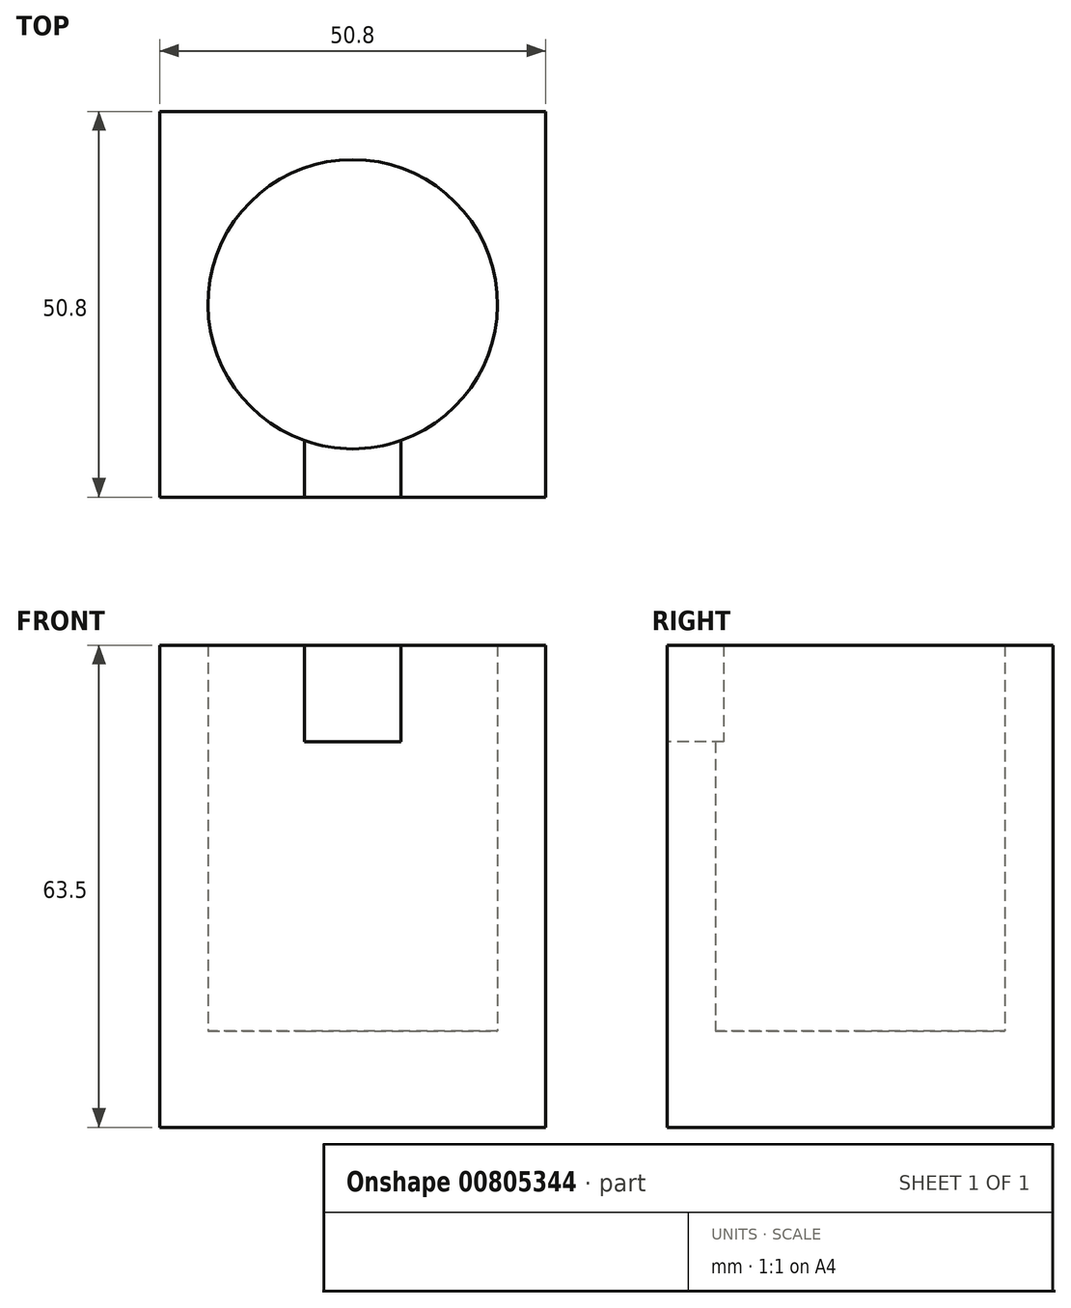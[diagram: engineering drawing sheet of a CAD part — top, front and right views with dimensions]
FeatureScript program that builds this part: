
annotation { "Feature Type Name" : "Feature", "Feature Type Description" : "" }
export const myFeature = defineFeature(function(context is Context, id is Id, definition is map)
    precondition{}
    {
        {
            var Q0;
            Q0=qCreatedBy(makeId("Top.planeOp"),FACE);
            var sketch = newSketch(context, id + "F0", { "sketchPlane" : qUnion([Q0])});
            skLineSegment(sketch, "E0.bottom", {"start": v(-50.8, 50.8) * mm, "end": v(0, 50.8) * mm});
            skLineSegment(sketch, "E0.top", {"start": v(-50.8, 0) * mm, "end": v(0, 0) * mm});
            skLineSegment(sketch, "E0.left", {"start": v(-50.8, 50.8) * mm, "end": v(-50.8, 0) * mm});
            skLineSegment(sketch, "E0.right", {"start": v(0, 50.8) * mm, "end": v(0, 0) * mm});
            skLineSegment(sketch, "E1", {"start": v(0, 25.4) * mm, "end": v(0, 0) * mm});
            skLineSegment(sketch, "E2", {"start": v(0, 0) * mm, "end": v(-25.4, 0) * mm});
            skCircle(sketch, "E3", {"center": v(-25.4, 25.4) * mm, "radius": 19.05 * mm});
            skSolve(sketch);
        }
        {
            var Q0;
            Q0=makeQuery(id+"F0.imprint","IMPRINT",FACE,{"disambiguationData":[TD([[makeQuery(id+"F0.imprint","IMPRINT",EDGE,{"derivedFrom":sQuery(id+"F0.wireOp",EDGE,"E0.bottom")}),-1.0]])]});
            extrude(context, id + "F1", {"entities" : qUnion([Q0]), "depth" : 63.5 * mm, "offsetDistance" : 25.4 * mm});
        }
        {
            var Q0;
            Q0=makeQuery(id+"F0.imprint","IMPRINT",FACE,{"disambiguationData":[TD([[makeQuery(id+"F0.imprint","IMPRINT",EDGE,{"derivedFrom":sQuery(id+"F0.wireOp",EDGE,"E3")}),1.0]])]});
            extrude(context, id + "F2", {"entities" : qUnion([Q0]), "operationType" : NewBodyOperationType.ADD, "depth" : 12.7 * mm, "offsetDistance" : 25.4 * mm});
        }
        {
            var Q0;
            Q0=makeQuery(id+"F1.opExtrude","SWEPT_FACE",FACE,{"disambiguationData":[OSD([sQuery(id+"F0.wireOp",EDGE,"E0.top"),sQuery(id+"F0.wireOp",EDGE,"E2")])]});
            var sketch = newSketch(context, id + "F3", { "sketchPlane" : qUnion([Q0])});
            skLineSegment(sketch, "E4", {"start": v(0, 63.5) * mm, "end": v(-25.4, 63.5) * mm});
            skLineSegment(sketch, "E5", {"start": v(-25.4, 63.5) * mm, "end": v(-19.05, 63.5) * mm});
            skLineSegment(sketch, "E6", {"start": v(-19.05, 63.5) * mm, "end": v(-25.4, 63.5) * mm});
            skLineSegment(sketch, "E7", {"start": v(-31.75, 63.5) * mm, "end": v(-25.4, 63.5) * mm});
            skLineSegment(sketch, "E8", {"start": v(-25.4, 63.5) * mm, "end": v(-25.4, 50.8) * mm});
            skLineSegment(sketch, "E9.top", {"start": v(-31.75, 50.8) * mm, "end": v(-25.4, 50.8) * mm});
            skLineSegment(sketch, "E9.left", {"start": v(-31.75, 63.5) * mm, "end": v(-31.75, 50.8) * mm});
            skLineSegment(sketch, "E10.bottom", {"start": v(-25.4, 50.8) * mm, "end": v(-19.05, 50.8) * mm});
            skLineSegment(sketch, "E10.right", {"start": v(-19.05, 50.8) * mm, "end": v(-19.05, 63.5) * mm});
            skLineSegment(sketch, "E11.bottom", {"start": v(-19.05, 50.8) * mm, "end": v(-31.75, 50.8) * mm});
            skLineSegment(sketch, "E11.top", {"start": v(-19.05, 63.5) * mm, "end": v(-31.75, 63.5) * mm});
            skLineSegment(sketch, "E11.right", {"start": v(-31.75, 50.8) * mm, "end": v(-31.75, 63.5) * mm});
            skSolve(sketch);
        }
        {
            var Q0;
            Q0 = qSketchRegion(id + "F3", true);
            extrude(context, id + "F4", {"entities" : qUnion([Q0]), "operationType" : NewBodyOperationType.REMOVE, "oppositeDirection" : true, "depth" : 7.62 * mm, "offsetDistance" : 25.4 * mm});
        }
    });
